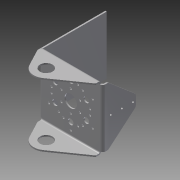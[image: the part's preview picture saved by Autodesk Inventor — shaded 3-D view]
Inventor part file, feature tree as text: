
AUTODESK INVENTOR PART (.ipt)
format: ipt  version: 2014 (Build 180170000, 170)  size: 400,896 bytes
history: native  units: in
note: dims shown in document units (in); Inventor stores cm internally (conversion verified against a paired STEP export)
features: sheet_metal_op x14, sketch x11, other x11, reference x4, fillet x2
ambient origin geometry x8: Origin, YZ Plane, XZ Plane, XY Plane, X Axis, Y Axis, Z Axis, Center Point
bodies: Solid1 (feature_tree)
feature tree (42):
  sheet_metal_op  "Face1"
  sheet_metal_op  "Flange2"
  sheet_metal_op  "Flange3"
  fillet  "Fillet2"  Radius=0.125in
  sheet_metal_op  "Flange4"
  sheet_metal_op  "Face2"
  sheet_metal_op  "Face3"
  fillet  "Fillet3"  Radius=0.125in
  sketch  "Sketch1"  dims[d1=2.3622in d2=5.25in d3=1.125in d4=0.503in d5=1.625in d6=1.31in d7=0.1875in d8=0.1875in d9=0.1875in d10=0.1875in d11=360.0deg d12=0.125in d23=0.125in]
  other  "Plate1"
  sketch  "Sketch3"  dims[d24=0.0625in]
  other  "Plate3"
  sheet_metal_op  "Bend2"
  sheet_metal_op  "Corner2"
  sketch  "Sketch5"  dims[d25=0.25in]
  reference  "Reference2"
  sketch  "Sketch7"  dims[d26=0.125in]
  other  "Plate4"
  sheet_metal_op  "Bend3"
  sheet_metal_op  "Corner3"
  sketch  "Sketch8"  dims[d27=3.0in d28=90.0deg d29=0.125in]
  sketch  "Sketch9"  dims[d30=0.5in]
  reference  "Reference3"
  reference  "Reference4"
  reference  "Reference5"
  sketch  "Sketch11"  dims[d31=0.125in]
  other  "Plate5"
  sheet_metal_op  "Bend4"
  sheet_metal_op  "Corner4"
  sketch  "Sketch13"  dims[d32=0.125in]
  sketch  "Sketch14"  dims[d39=1.125in]
  other  "Plate6"
  sheet_metal_op  "Bend5"
  sketch  "Sketch15"  dims[d40=100.0in d41=0.0in]
  other  "Plate7"
  sheet_metal_op  "Bend6"
  sketch  "Sketch17"  dims[d48=0.125in d49=0.0625in d50=0.25in d51=0.125in d52=3.0in d53=90.0deg d54=0.125in d55=0.5in d56=0.125in d57=0.125in d58=1.0in d59=2.125in d60=0.25in d61=0.25in d62=0.125in d63=0.0in d64=0.25in d65=0.164in d66=0.164in d67=0.164in d68=0.125in d69=0.0in d71=0.125in d72=0.0625in d73=0.25in d74=0.125in d75=6.25in d76=90.0deg d77=0.125in d78=0.5in d79=0.125in d80=0.125in d81=1.0in d82=1.0in d83=2.125in d84=0.125in d85=0.0in d86=2.5in d87=0.125in d88=0.125in d89=0.0625in d90=0.25in d91=0.125in d92=2.5in d93=2.75in d94=0.125in d95=0.125in d96=0.0625in d97=0.25in d98=0.125in d100=0.25in d101=0.5in d102=1.0in d103=0.5in d104=0.5in d105=0.5in d106=1.0in d107=1.0in d108=0.25in d109=0.25in d110=0.25in d111=0.25in d112=0.125in d113=0.125in d114=0.25in d115=0.25in d116=0.25in d117=0.25in d118=0.125in d119=0.125in d120=0.125in d121=0.125in d122=0.125in d123=0.125in d124=0.125in d125=0.125in d127=0.5in d128=0.125in d129=0.125in d130=0.0in]
  other  "Cut2"
  other  "Cut4"
  other  "Cut5"
  other  "Cut6"
  other  "Cut7"
